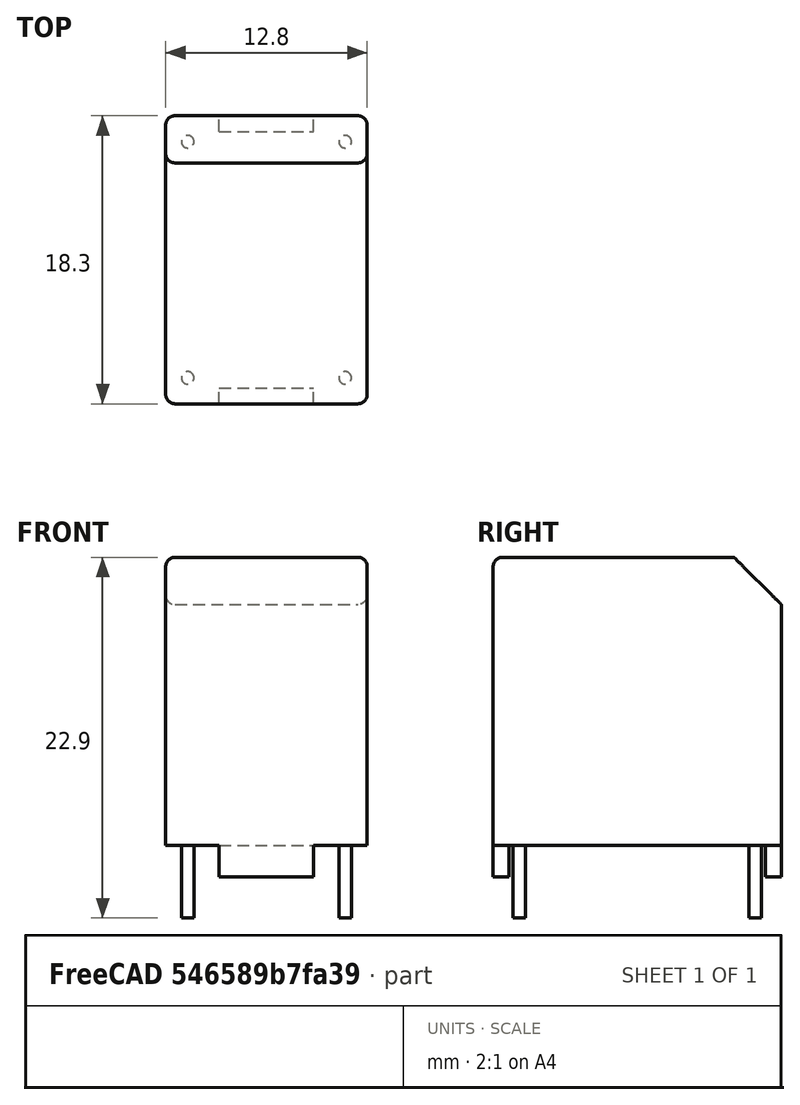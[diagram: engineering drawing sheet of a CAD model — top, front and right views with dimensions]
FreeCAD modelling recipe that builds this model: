
FCSTD DOCUMENT
Label: SCHAFFNER_RN212
objects: Part::Box×4, Part::Cylinder×4, Part::Cut×3, PartDesign::Chamfer×1, Part::Fillet×1, Part::MultiFuse×1
note: 14 computed .brp shape members not serialized (recipe doc carries the construction recipe); baked Part::Feature solids carry a one-line shape summary decoded from their .brp

FEATURE [Part::Box] Box
  Height = 20.3
  Length = 12.8
  Width = 18.3
FEATURE [Part::Box] Box001  label="left_cutout"
  Height = 2
  Length = 3.4
  Width = 18.3
FEATURE [Part::Box] Box002  label="right_cutout"
  Height = 2
  Length = 3.4
  Placement = pos=(9.4,0,0) rot=(0,0,1;0rad)
  Width = 18.3
FEATURE [Part::Cut] Cut
  Base = -> Box
  Tool = -> Box001
FEATURE [Part::Cut] Cut001
  Base = -> Cut
  Tool = -> Box002
FEATURE [Part::Box] Box003
  Height = 2
  Length = 12.8
  Placement = pos=(0,1,0) rot=(0,0,1;0rad)
  Width = 16.3
FEATURE [Part::Cut] Cut002  label="Grundkoerper_Block"
  Base = -> Cut001
  Tool = -> Box003
FEATURE [PartDesign::Chamfer] Chamfer
  Base = -> Cut002 [Edge2]
  Size = 3
FEATURE [Part::Fillet] Fillet  label="Grundkoerper_Abgerundet"
  Base = -> Chamfer
  Edges = 7 edges r=0.6: [Edge1,Edge3,Edge4,Edge6,Edge7,Edge16,Edge19]
FEATURE [Part::Cylinder] Cylinder  label="Pin4"
  Angle = 360
  Height = 4.6
  Placement = pos=(1.4,1.65,-2.6) rot=(0,0,1;0rad)
  Radius = 0.4
FEATURE [Part::Cylinder] Cylinder001  label="Pin3"
  Angle = 360
  Height = 4.6
  Placement = pos=(11.4,1.65,-2.6) rot=(0,0,1;0rad)
  Radius = 0.4
FEATURE [Part::Cylinder] Cylinder002  label="Pin2"
  Angle = 360
  Height = 4.6
  Placement = pos=(11.4,16.65,-2.6) rot=(0,0,1;0rad)
  Radius = 0.4
FEATURE [Part::Cylinder] Cylinder003  label="Pin1"
  Angle = 360
  Height = 4.6
  Placement = pos=(1.4,16.65,-2.6) rot=(0,0,1;0rad)
  Radius = 0.4
FEATURE [Part::MultiFuse] Fusion  label="RN212"
  Shapes = -> [Fillet,Cylinder,Cylinder001,Cylinder002,Cylinder003]
